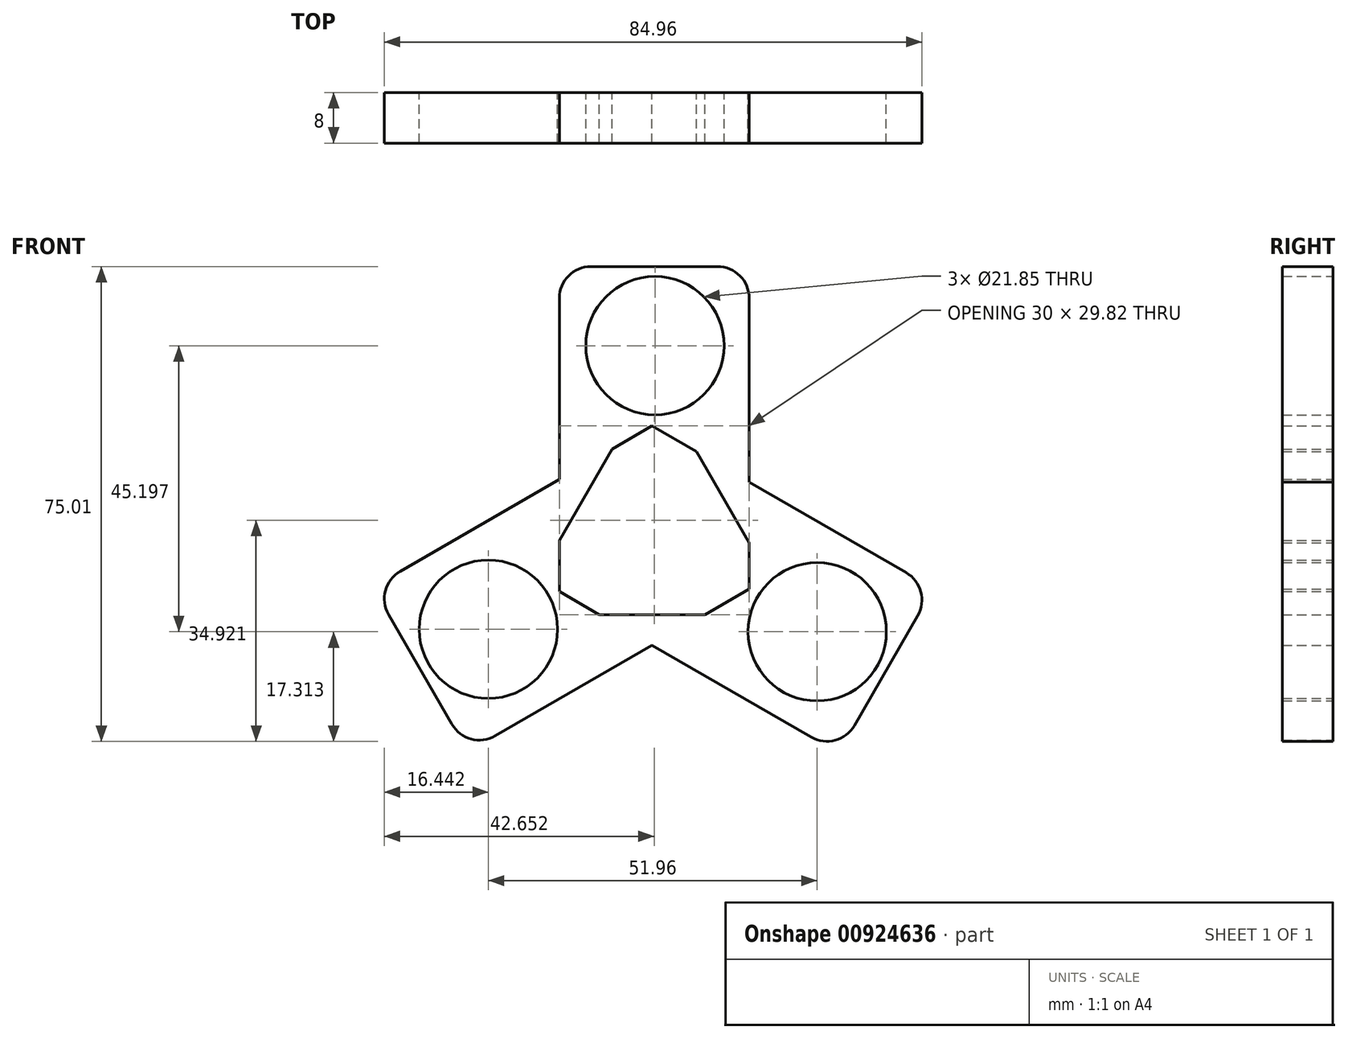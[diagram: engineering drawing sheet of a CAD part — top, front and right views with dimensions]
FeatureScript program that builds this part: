
annotation { "Feature Type Name" : "Feature", "Feature Type Description" : "" }
export const myFeature = defineFeature(function(context is Context, id is Id, definition is map)
    precondition{}
    {
        {
            var Q0;
            Q0=qCreatedBy(makeId("Front.planeOp"),FACE);
            var sketch = newSketch(context, id + "F0", { "sketchPlane" : qUnion([Q0])});
            skCircle(sketch, "E0", {"center": v(-151.43, 4.31) * mm, "radius": 10.93 * mm});
            skCircle(sketch, "E1", {"center": v(-151.2, 34.31) * mm, "radius": 10.93 * mm});
            skLineSegment(sketch, "E2", {"start": v(-151.2, 34.31) * mm, "end": v(-151.43, 4.31) * mm, "construction": true});
            skLineSegment(sketch, "E3.bottom", {"start": v(-136.32, -8.19) * mm, "end": v(-166.32, -8.19) * mm});
            skLineSegment(sketch, "E3.top", {"start": v(-141.32, 46.81) * mm, "end": v(-161.32, 46.81) * mm});
            skLineSegment(sketch, "E3.left", {"start": v(-136.32, -8.19) * mm, "end": v(-136.32, 41.81) * mm});
            skLineSegment(sketch, "E3.right", {"start": v(-166.32, -8.19) * mm, "end": v(-166.32, 41.81) * mm});
            skPoint(sketch, "E3.middle", {"position": v(-151.32, 19.31) * mm});
            skPoint(sketch, "E4.visualSharp", {"position": v(-166.32, 46.81) * mm});
            skArc(sketch, "E4.filletArc", {"start": v(-161.32, 46.81) * mm, "mid": v(-164.85, 45.35) * mm, "end": v(-166.32, 41.81) * mm});
            skPoint(sketch, "E5.visualSharp", {"position": v(-136.32, 46.81) * mm});
            skArc(sketch, "E5.filletArc", {"start": v(-136.32, 41.81) * mm, "mid": v(-137.78, 45.35) * mm, "end": v(-141.32, 46.81) * mm});
            skPoint(sketch, "E6.1.0", {"position": v(-164.48, -3.09) * mm});
            skPoint(sketch, "E6.2.0", {"position": v(-138.5, -3.29) * mm});
            skCircle(sketch, "E7.1.0", {"center": v(-177.53, -10.5) * mm, "radius": 10.93 * mm});
            skLineSegment(sketch, "E7.1.1", {"start": v(-133.16, -2.33) * mm, "end": v(-176.47, -27.33) * mm});
            skLineSegment(sketch, "E7.1.2", {"start": v(-193.3, -8.18) * mm, "end": v(-183.3, -25.5) * mm});
            skPoint(sketch, "E7.1.6", {"position": v(-195.8, -3.85) * mm});
            skPoint(sketch, "E7.1.7", {"position": v(-180.8, -29.83) * mm});
            skLineSegment(sketch, "E7.1.9", {"start": v(-177.53, -10.5) * mm, "end": v(-151.43, 4.31) * mm, "construction": true});
            skLineSegment(sketch, "E7.1.11", {"start": v(-148.16, 23.65) * mm, "end": v(-133.16, -2.33) * mm});
            skLineSegment(sketch, "E7.1.12", {"start": v(-148.16, 23.65) * mm, "end": v(-191.47, -1.35) * mm});
            skArc(sketch, "E7.1.13", {"start": v(-191.47, -1.35) * mm, "mid": v(-193.8, -4.39) * mm, "end": v(-193.3, -8.18) * mm});
            skArc(sketch, "E7.1.14", {"start": v(-183.3, -25.5) * mm, "mid": v(-180.26, -27.83) * mm, "end": v(-176.47, -27.33) * mm});
            skCircle(sketch, "E7.2.0", {"center": v(-125.57, -10.89) * mm, "radius": 10.93 * mm});
            skLineSegment(sketch, "E7.2.1", {"start": v(-154.82, 23.45) * mm, "end": v(-111.51, -1.55) * mm});
            skLineSegment(sketch, "E7.2.2", {"start": v(-119.68, -25.7) * mm, "end": v(-109.68, -8.38) * mm});
            skPoint(sketch, "E7.2.6", {"position": v(-122.18, -30.03) * mm});
            skPoint(sketch, "E7.2.7", {"position": v(-107.18, -4.05) * mm});
            skLineSegment(sketch, "E7.2.9", {"start": v(-125.57, -10.89) * mm, "end": v(-151.43, 4.31) * mm, "construction": true});
            skLineSegment(sketch, "E7.2.11", {"start": v(-169.82, -2.53) * mm, "end": v(-154.82, 23.45) * mm});
            skLineSegment(sketch, "E7.2.12", {"start": v(-169.82, -2.53) * mm, "end": v(-126.51, -27.53) * mm});
            skArc(sketch, "E7.2.13", {"start": v(-126.51, -27.53) * mm, "mid": v(-122.72, -28.03) * mm, "end": v(-119.68, -25.7) * mm});
            skArc(sketch, "E7.2.14", {"start": v(-109.68, -8.38) * mm, "mid": v(-109.19, -4.58) * mm, "end": v(-111.51, -1.55) * mm});
            skSolve(sketch);
        }
        {
            var Q0;
            Q0=makeQuery(id+"F0.imprint","IMPRINT",FACE,{"disambiguationData":[TD([[makeQuery(id+"F0.imprint","IMPRINT",EDGE,{"derivedFrom":sQuery(id+"F0.wireOp",EDGE,"E7.2.0")}),-1.0]])]});
            var Q1;
            {var subQ0=sQuery(id+"F0.wireOp",EDGE,"E7.2.1");var subQ1=sQuery(id+"F0.wireOp",EDGE,"E3.left");var subQ2=makeQuery(id+"F0.imprint","INTERSECT",VERTEX,{"derivedFrom":[subQ1,subQ0]});Q1=makeQuery(id+"F0.imprint","IMPRINT",FACE,{"disambiguationData":[TD([[makeQuery(id+"F0.imprint","IMPRINT",EDGE,{"disambiguationData":[TD([[subQ2,1.0]])],"derivedFrom":subQ1}),1.0]])]});}
            var Q2;
            {var subQ0=sQuery(id+"F0.wireOp",EDGE,"E7.2.1");var subQ1=sQuery(id+"F0.wireOp",EDGE,"E7.1.12");var subQ2=makeQuery(id+"F0.imprint","INTERSECT",VERTEX,{"derivedFrom":[subQ1,subQ0]});Q2=makeQuery(id+"F0.imprint","IMPRINT",FACE,{"disambiguationData":[TD([[makeQuery(id+"F0.imprint","IMPRINT",EDGE,{"disambiguationData":[TD([[subQ2,-1.0]])],"derivedFrom":subQ1}),-1.0]])]});}
            var Q3;
            Q3=makeQuery(id+"F0.imprint","IMPRINT",FACE,{"disambiguationData":[TD([[makeQuery(id+"F0.imprint","IMPRINT",EDGE,{"derivedFrom":sQuery(id+"F0.wireOp",EDGE,"E1")}),-1.0]])]});
            var Q4;
            {var subQ0=sQuery(id+"F0.wireOp",EDGE,"E7.1.12");var subQ1=sQuery(id+"F0.wireOp",EDGE,"E3.right");var subQ2=makeQuery(id+"F0.imprint","INTERSECT",VERTEX,{"derivedFrom":[subQ1,subQ0]});Q4=makeQuery(id+"F0.imprint","IMPRINT",FACE,{"disambiguationData":[TD([[makeQuery(id+"F0.imprint","IMPRINT",EDGE,{"disambiguationData":[TD([[subQ2,1.0]])],"derivedFrom":subQ1}),-1.0]])]});}
            var Q5;
            Q5=makeQuery(id+"F0.imprint","IMPRINT",FACE,{"disambiguationData":[TD([[makeQuery(id+"F0.imprint","IMPRINT",EDGE,{"derivedFrom":sQuery(id+"F0.wireOp",EDGE,"E7.1.0")}),-1.0]])]});
            var Q6;
            Q6=makeQuery(id+"F0.imprint","IMPRINT",FACE,{"disambiguationData":[TD([[makeQuery(id+"F0.imprint","IMPRINT",EDGE,{"derivedFrom":sQuery(id+"F0.wireOp",EDGE,"E0")}),-1.0]])]});
            var Q7;
            {var subQ0=sQuery(id+"F0.wireOp",EDGE,"E7.2.12");var subQ1=sQuery(id+"F0.wireOp",EDGE,"E3.right");var subQ2=makeQuery(id+"F0.imprint","INTERSECT",VERTEX,{"derivedFrom":[subQ1,subQ0]});Q7=makeQuery(id+"F0.imprint","IMPRINT",FACE,{"disambiguationData":[TD([[makeQuery(id+"F0.imprint","IMPRINT",EDGE,{"disambiguationData":[TD([[subQ2,-1.0]])],"derivedFrom":subQ1}),1.0]])]});}
            var Q8;
            {var subQ0=sQuery(id+"F0.wireOp",EDGE,"E7.1.12");var subQ1=sQuery(id+"F0.wireOp",EDGE,"E7.1.11");var subQ2=makeQuery(id+"F0.imprint","INTERSECT",VERTEX,{"derivedFrom":[subQ1,subQ0]});Q8=makeQuery(id+"F0.imprint","IMPRINT",FACE,{"disambiguationData":[TD([[makeQuery(id+"F0.imprint","IMPRINT",EDGE,{"disambiguationData":[TD([[subQ2,-1.0]])],"derivedFrom":subQ1}),-1.0]])]});}
            var Q9;
            {var subQ0=sQuery(id+"F0.wireOp",EDGE,"E7.1.1");var subQ1=sQuery(id+"F0.wireOp",EDGE,"E3.left");var subQ2=makeQuery(id+"F0.imprint","INTERSECT",VERTEX,{"derivedFrom":[subQ1,subQ0]});Q9=makeQuery(id+"F0.imprint","IMPRINT",FACE,{"disambiguationData":[TD([[makeQuery(id+"F0.imprint","IMPRINT",EDGE,{"disambiguationData":[TD([[subQ2,-1.0]])],"derivedFrom":subQ1}),-1.0]])]});}
            var Q10;
            {var subQ0=sQuery(id+"F0.wireOp",EDGE,"E3.left");var subQ1=sQuery(id+"F0.wireOp",EDGE,"E3.bottom");var subQ2=makeQuery(id+"F0.imprint","INTERSECT",VERTEX,{"derivedFrom":[subQ1,subQ0]});Q10=makeQuery(id+"F0.imprint","IMPRINT",FACE,{"disambiguationData":[TD([[makeQuery(id+"F0.imprint","IMPRINT",EDGE,{"disambiguationData":[TD([[subQ2,-1.0]])],"derivedFrom":subQ1}),-1.0]])]});}
            var Q11;
            {var subQ0=sQuery(id+"F0.wireOp",EDGE,"E3.right");var subQ1=sQuery(id+"F0.wireOp",EDGE,"E3.bottom");var subQ2=makeQuery(id+"F0.imprint","INTERSECT",VERTEX,{"derivedFrom":[subQ1,subQ0]});Q11=makeQuery(id+"F0.imprint","IMPRINT",FACE,{"disambiguationData":[TD([[makeQuery(id+"F0.imprint","IMPRINT",EDGE,{"disambiguationData":[TD([[subQ2,1.0]])],"derivedFrom":subQ1}),-1.0]])]});}
            var Q12;
            {var subQ0=sQuery(id+"F0.wireOp",EDGE,"E7.1.1");var subQ1=sQuery(id+"F0.wireOp",EDGE,"E3.bottom");var subQ2=makeQuery(id+"F0.imprint","INTERSECT",VERTEX,{"derivedFrom":[subQ1,subQ0]});Q12=makeQuery(id+"F0.imprint","IMPRINT",FACE,{"disambiguationData":[TD([[makeQuery(id+"F0.imprint","IMPRINT",EDGE,{"disambiguationData":[TD([[subQ2,-1.0]])],"derivedFrom":subQ1}),1.0]])]});}
            extrude(context, id + "F1", {"entities" : qUnion([Q0, Q1, Q2, Q3, Q4, Q5, Q6, Q7, Q8, Q9, Q10, Q11, Q12]), "depth" : 8 * mm, "offsetDistance" : 25 * mm});
        }
    });
